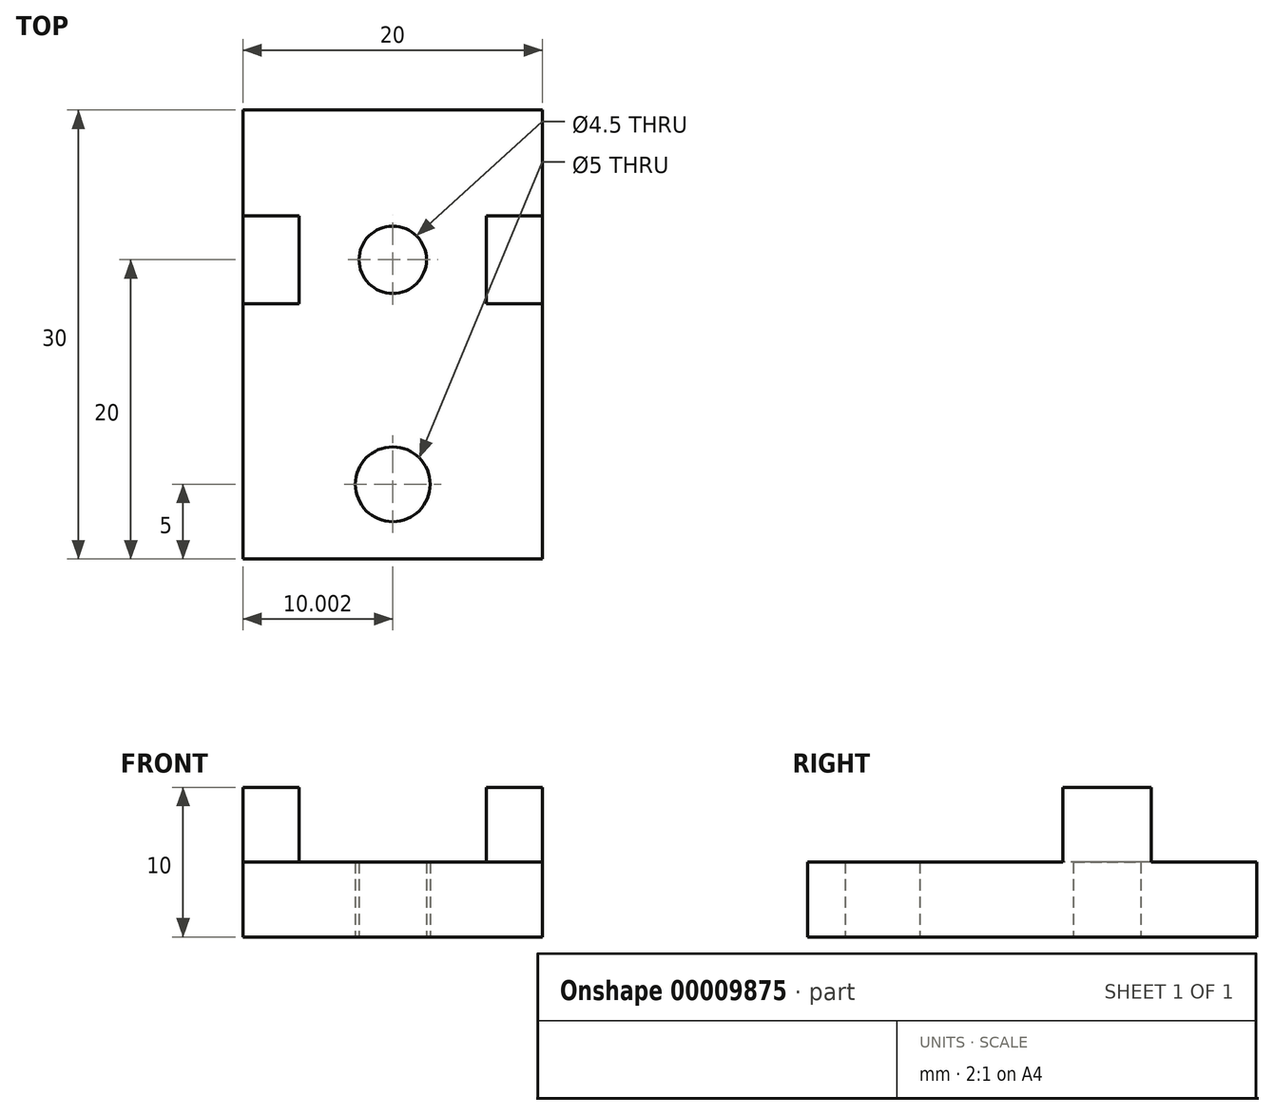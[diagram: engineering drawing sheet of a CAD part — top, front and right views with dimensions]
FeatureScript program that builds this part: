
annotation { "Feature Type Name" : "Feature", "Feature Type Description" : "" }
export const myFeature = defineFeature(function(context is Context, id is Id, definition is map)
    precondition{}
    {
        {
            var Q0;
            Q0=qCreatedBy(makeId("Top.planeOp"),FACE);
            var sketch = newSketch(context, id + "F0", { "sketchPlane" : qUnion([Q0])});
            skLineSegment(sketch, "E0.bottom", {"start": v(-18.76, 0) * mm, "end": v(1.24, 0) * mm});
            skLineSegment(sketch, "E0.top", {"start": v(-18.76, 30) * mm, "end": v(1.24, 30) * mm});
            skLineSegment(sketch, "E0.left", {"start": v(-18.76, 0) * mm, "end": v(-18.76, 30) * mm});
            skLineSegment(sketch, "E0.right", {"start": v(1.24, 0) * mm, "end": v(1.24, 30) * mm});
            skLineSegment(sketch, "E1", {"start": v(-18.76, 10) * mm, "end": v(1.24, 10) * mm});
            skCircle(sketch, "E2", {"center": v(-8.76, 5) * mm, "radius": 2.5 * mm});
            skCircle(sketch, "E3", {"center": v(-8.76, 20) * mm, "radius": 2.25 * mm});
            skPoint(sketch, "E4", {"position": v(-8.76, 30) * mm});
            skLineSegment(sketch, "E5.bottom", {"start": v(-18.76, 22.95) * mm, "end": v(-15, 22.95) * mm});
            skLineSegment(sketch, "E5.top", {"start": v(-18.76, 17.05) * mm, "end": v(-15, 17.05) * mm});
            skLineSegment(sketch, "E5.left", {"start": v(-18.76, 22.95) * mm, "end": v(-18.76, 17.05) * mm});
            skLineSegment(sketch, "E5.right", {"start": v(-15, 22.95) * mm, "end": v(-15, 17.05) * mm});
            skLineSegment(sketch, "E6.bottom", {"start": v(1.24, 22.95) * mm, "end": v(-2.5, 22.95) * mm});
            skLineSegment(sketch, "E6.top", {"start": v(1.24, 17.05) * mm, "end": v(-2.5, 17.05) * mm});
            skLineSegment(sketch, "E6.left", {"start": v(1.24, 22.95) * mm, "end": v(1.24, 17.05) * mm});
            skLineSegment(sketch, "E6.right", {"start": v(-2.5, 22.95) * mm, "end": v(-2.5, 17.05) * mm});
            skPoint(sketch, "E7", {"position": v(-15, 20) * mm});
            skSolve(sketch);
        }
        {
            var Q0;
            {var subQ6=sQuery(id+"F0.wireOp",EDGE,"E0.top");Q0=makeQuery(id+"F0.imprint","IMPRINT",FACE,{"disambiguationData":[TD([[makeQuery(id+"F0.imprint","IMPRINT",EDGE,{"derivedFrom":subQ6}),-1.0]])]});}
            var Q1;
            {var subQ2=sQuery(id+"F0.wireOp",EDGE,"E0.bottom");Q1=makeQuery(id+"F0.imprint","IMPRINT",FACE,{"disambiguationData":[TD([[makeQuery(id+"F0.imprint","IMPRINT",EDGE,{"derivedFrom":subQ2}),1.0]])]});}
            extrude(context, id + "F1", {"entities" : qUnion([Q0, Q1]), "depth" : 5 * mm});
        }
        {
            var Q0;
            Q0=makeQuery(id+"F0.imprint","IMPRINT",FACE,{"disambiguationData":[TD([[makeQuery(id+"F0.imprint","IMPRINT",EDGE,{"derivedFrom":sQuery(id+"F0.wireOp",EDGE,"E5.bottom")}),-1.0]])]});
            var Q1;
            Q1=makeQuery(id+"F0.imprint","IMPRINT",FACE,{"disambiguationData":[TD([[makeQuery(id+"F0.imprint","IMPRINT",EDGE,{"derivedFrom":sQuery(id+"F0.wireOp",EDGE,"E6.bottom")}),1.0]])]});
            extrude(context, id + "F2", {"entities" : qUnion([Q0, Q1]), "operationType" : NewBodyOperationType.ADD, "depth" : 10 * mm});
        }
    });
